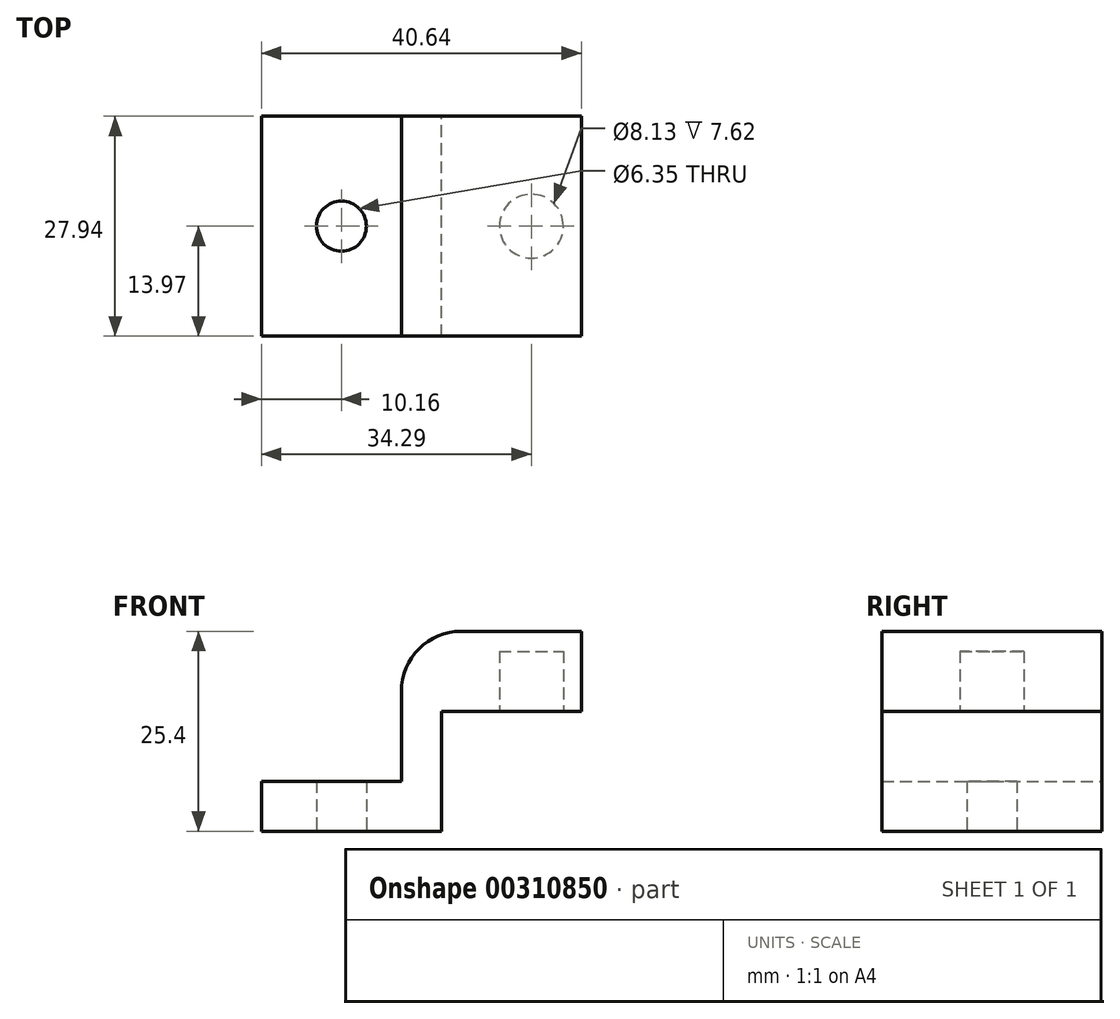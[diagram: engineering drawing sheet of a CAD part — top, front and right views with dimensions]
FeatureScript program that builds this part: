
annotation { "Feature Type Name" : "Feature", "Feature Type Description" : "" }
export const myFeature = defineFeature(function(context is Context, id is Id, definition is map)
    precondition{}
    {
        {
            var Q0;
            Q0=qCreatedBy(makeId("Front.planeOp"),FACE);
            var sketch = newSketch(context, id + "F0", { "sketchPlane" : qUnion([Q0])});
            skLineSegment(sketch, "E0", {"start": v(0, 0) * mm, "end": v(0, 15.24) * mm});
            skLineSegment(sketch, "E1", {"start": v(0, 15.24) * mm, "end": v(17.78, 15.24) * mm});
            skLineSegment(sketch, "E2", {"start": v(17.78, 15.24) * mm, "end": v(17.78, 25.4) * mm});
            skLineSegment(sketch, "E3", {"start": v(17.78, 25.4) * mm, "end": v(-5.08, 25.4) * mm});
            skLineSegment(sketch, "E4", {"start": v(-5.08, 25.4) * mm, "end": v(-5.08, 6.35) * mm});
            skLineSegment(sketch, "E5", {"start": v(-5.08, 6.35) * mm, "end": v(-22.86, 6.35) * mm});
            skLineSegment(sketch, "E6", {"start": v(-22.86, 6.35) * mm, "end": v(-22.86, 0) * mm});
            skLineSegment(sketch, "E7", {"start": v(-22.86, 0) * mm, "end": v(0, 0) * mm});
            skSolve(sketch);
        }
        {
            var Q0;
            Q0 = qSketchRegion(id + "F0", true);
            extrude(context, id + "F1", {"entities" : qUnion([Q0]), "depth" : 27.94 * mm});
        }
        {
            var Q0;
            Q0=makeQuery(id+"F1.opExtrude","SWEPT_FACE",FACE,{"disambiguationData":[OSD([sQuery(id+"F0.wireOp",EDGE,"E1")])]});
            var sketch = newSketch(context, id + "F2", { "sketchPlane" : qUnion([Q0])});
            skCircle(sketch, "E8", {"center": v(11.43, 13.97) * mm, "radius": 4.06 * mm});
            skLineSegment(sketch, "E9", {"start": v(11.43, 27.94) * mm, "end": v(11.43, 0) * mm});
            skPoint(sketch, "E9.endSnap0", {"position": v(8.9, 0) * mm});
            skSolve(sketch);
        }
        {
            var Q0;
            Q0 = qSketchRegion(id + "F2", true);
            extrude(context, id + "F3", {"entities" : qUnion([Q0]), "operationType" : NewBodyOperationType.REMOVE, "oppositeDirection" : true, "depth" : 7.62 * mm});
        }
        {
            var Q0;
            Q0=makeQuery(id+"F1.opExtrude","SWEPT_EDGE",EDGE,{"disambiguationData":[OSD([sQuery(id+"F0.wireOp",EDGE,"E3"),sQuery(id+"F0.wireOp",EDGE,"E4")])]});
            fillet(context, id + "F4", {"entities" : qUnion([Q0]), "radius" : 7.62 * mm, "tangentPropagation" : true, "allowEdgeOverflow" : false});
        }
        {
            var Q0;
            Q0=makeQuery(id+"F1.opExtrude","SWEPT_FACE",FACE,{"disambiguationData":[OSD([sQuery(id+"F0.wireOp",EDGE,"E7")])]});
            var sketch = newSketch(context, id + "F5", { "sketchPlane" : qUnion([Q0])});
            skCircle(sketch, "E10", {"center": v(-12.7, 13.97) * mm, "radius": 3.18 * mm});
            skSolve(sketch);
        }
        {
            var Q0;
            Q0 = qSketchRegion(id + "F5", true);
            extrude(context, id + "F6", {"entities" : qUnion([Q0]), "operationType" : NewBodyOperationType.REMOVE, "oppositeDirection" : true, "depth" : 25.4 * mm});
        }
    });
